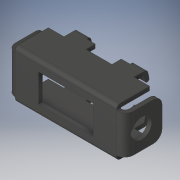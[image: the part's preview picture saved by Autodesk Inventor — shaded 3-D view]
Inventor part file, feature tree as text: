
AUTODESK INVENTOR PART (.ipt)
format: ipt  version: 2019.4 (Build 234330000, 330)  size: 240,640 bytes
history: native  units: mm
features: other x3, sketch x2
ambient origin geometry x8: Origin, YZ Plane, XZ Plane, XY Plane, X Axis, Y Axis, Z Axis, Center Point
bodies: Solid1 (feature_tree)
feature tree (5):
  other  "Bend Part1"
  other  "Bend Part2"
  sketch  "Sketch1"  dims[d0=0.5mm d1=90.0deg]
  sketch  "Sketch3"  dims[d2=0.5mm d3=90.0deg]
  other  "PartBody"
